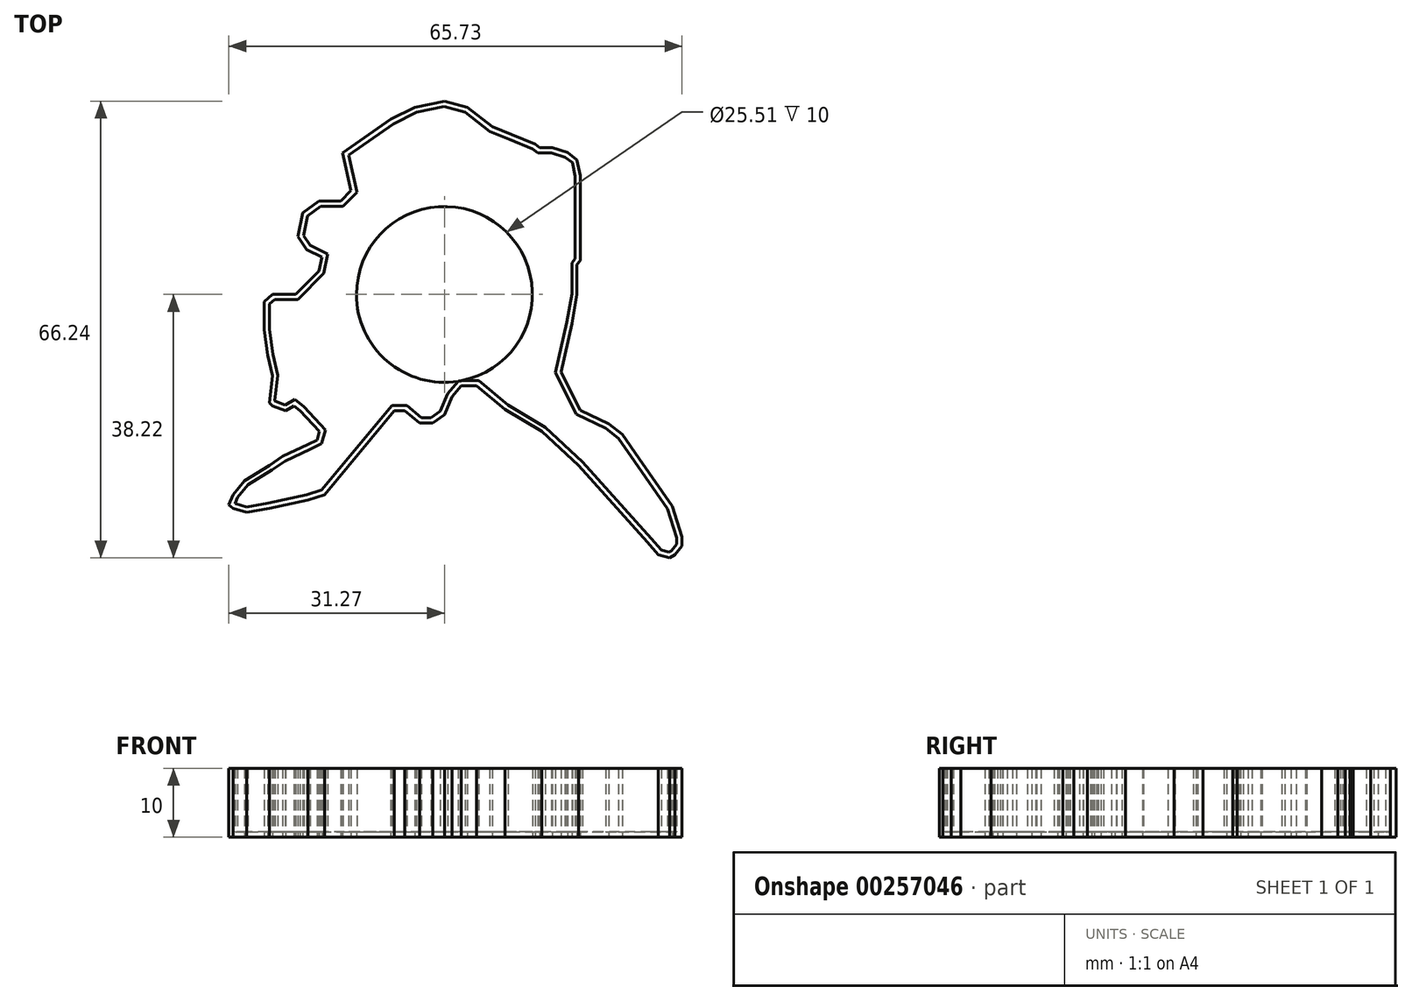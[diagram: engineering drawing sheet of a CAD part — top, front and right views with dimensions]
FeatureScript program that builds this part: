
annotation { "Feature Type Name" : "Feature", "Feature Type Description" : "" }
export const myFeature = defineFeature(function(context is Context, id is Id, definition is map)
    precondition{}
    {
        {
            var Q0;
            Q0=qCreatedBy(makeId("Top.planeOp"),FACE);
            var sketch = newSketch(context, id + "F0", { "sketchPlane" : qUnion([Q0])});
            skLineSegment(sketch, "E0", {"start": v(-14.76, 20.56) * mm, "end": v(-7.8, 25.4) * mm});
            skLineSegment(sketch, "E1", {"start": v(-7.8, 25.4) * mm, "end": v(-4.28, 27.17) * mm});
            skLineSegment(sketch, "E2", {"start": v(-4.28, 27.17) * mm, "end": v(0, 28.02) * mm});
            skLineSegment(sketch, "E3", {"start": v(0, 28.02) * mm, "end": v(3.33, 27.17) * mm});
            skLineSegment(sketch, "E4", {"start": v(3.33, 27.17) * mm, "end": v(6.95, 24.32) * mm});
            skLineSegment(sketch, "E5", {"start": v(6.95, 24.32) * mm, "end": v(9.72, 23.22) * mm});
            skLineSegment(sketch, "E6", {"start": v(9.72, 23.22) * mm, "end": v(13.2, 21.8) * mm});
            skLineSegment(sketch, "E7", {"start": v(13.2, 21.8) * mm, "end": v(13.8, 21.31) * mm});
            skLineSegment(sketch, "E8", {"start": v(13.8, 21.31) * mm, "end": v(15.64, 21.31) * mm});
            skLineSegment(sketch, "E9", {"start": v(15.64, 21.31) * mm, "end": v(17.85, 20.61) * mm});
            skLineSegment(sketch, "E10", {"start": v(17.85, 20.61) * mm, "end": v(19.23, 19.53) * mm});
            skLineSegment(sketch, "E11", {"start": v(19.23, 19.53) * mm, "end": v(19.69, 17.22) * mm});
            skLineSegment(sketch, "E12", {"start": v(19.69, 17.22) * mm, "end": v(19.69, 14.5) * mm});
            skLineSegment(sketch, "E13", {"start": v(19.69, 14.5) * mm, "end": v(19.69, 10.18) * mm});
            skLineSegment(sketch, "E14", {"start": v(19.69, 10.18) * mm, "end": v(19.69, 4.9) * mm});
            skLineSegment(sketch, "E15", {"start": v(19.69, 4.9) * mm, "end": v(19.23, 4.32) * mm});
            skLineSegment(sketch, "E16", {"start": v(19.23, 4.32) * mm, "end": v(19.23, 0) * mm});
            skLineSegment(sketch, "E17", {"start": v(19.23, 0) * mm, "end": v(18.47, -4.21) * mm});
            skLineSegment(sketch, "E18", {"start": v(18.47, -4.21) * mm, "end": v(16.88, -11.27) * mm});
            skLineSegment(sketch, "E19", {"start": v(16.88, -11.27) * mm, "end": v(19.69, -16.78) * mm});
            skLineSegment(sketch, "E20", {"start": v(19.69, -16.78) * mm, "end": v(23.8, -18.77) * mm});
            skLineSegment(sketch, "E21", {"start": v(23.8, -18.77) * mm, "end": v(25.8, -20.33) * mm});
            skLineSegment(sketch, "E22", {"start": v(25.8, -20.33) * mm, "end": v(28.2, -23.8) * mm});
            skLineSegment(sketch, "E23", {"start": v(28.2, -23.8) * mm, "end": v(33.02, -30.73) * mm});
            skLineSegment(sketch, "E24", {"start": v(33.02, -30.73) * mm, "end": v(34.46, -35.15) * mm});
            skLineSegment(sketch, "E25", {"start": v(34.46, -35.15) * mm, "end": v(34.46, -36.52) * mm});
            skLineSegment(sketch, "E26", {"start": v(34.46, -36.52) * mm, "end": v(33.4, -37.77) * mm});
            skLineSegment(sketch, "E27", {"start": v(33.4, -37.77) * mm, "end": v(32.64, -38.22) * mm});
            skLineSegment(sketch, "E28", {"start": v(32.64, -38.22) * mm, "end": v(31.03, -37.77) * mm});
            skLineSegment(sketch, "E29", {"start": v(31.03, -37.77) * mm, "end": v(29.4, -35.93) * mm});
            skLineSegment(sketch, "E30", {"start": v(29.4, -35.93) * mm, "end": v(19.48, -24.82) * mm});
            skLineSegment(sketch, "E31", {"start": v(19.48, -24.82) * mm, "end": v(14.15, -19.87) * mm});
            skLineSegment(sketch, "E32", {"start": v(14.15, -19.87) * mm, "end": v(8.79, -16.69) * mm});
            skLineSegment(sketch, "E33", {"start": v(8.79, -16.69) * mm, "end": v(4.67, -13.27) * mm});
            skLineSegment(sketch, "E34", {"start": v(4.67, -13.27) * mm, "end": v(2.4, -13.27) * mm});
            skLineSegment(sketch, "E35", {"start": v(2.4, -13.27) * mm, "end": v(1.12, -14.82) * mm});
            skLineSegment(sketch, "E36", {"start": v(1.12, -14.82) * mm, "end": v(0, -17.42) * mm});
            skLineSegment(sketch, "E37", {"start": v(0, -17.42) * mm, "end": v(-1.7, -18.66) * mm});
            skLineSegment(sketch, "E38", {"start": v(-1.7, -18.66) * mm, "end": v(-3.6, -18.66) * mm});
            skLineSegment(sketch, "E39", {"start": v(-3.6, -18.66) * mm, "end": v(-5.74, -16.88) * mm});
            skLineSegment(sketch, "E40", {"start": v(-5.74, -16.88) * mm, "end": v(-7.25, -16.88) * mm});
            skLineSegment(sketch, "E41", {"start": v(-7.25, -16.88) * mm, "end": v(-11.3, -21.74) * mm});
            skLineSegment(sketch, "E42", {"start": v(-11.3, -21.74) * mm, "end": v(-12.76, -23.5) * mm});
            skLineSegment(sketch, "E43", {"start": v(-12.76, -23.5) * mm, "end": v(-16.11, -27.53) * mm});
            skLineSegment(sketch, "E44", {"start": v(-16.11, -27.53) * mm, "end": v(-17.36, -29.04) * mm});
            skLineSegment(sketch, "E45", {"start": v(-17.36, -29.04) * mm, "end": v(-19.79, -29.82) * mm});
            skLineSegment(sketch, "E46", {"start": v(-19.79, -29.82) * mm, "end": v(-25.4, -31) * mm});
            skLineSegment(sketch, "E47", {"start": v(-25.4, -31) * mm, "end": v(-28.7, -31.63) * mm});
            skLineSegment(sketch, "E48", {"start": v(-28.7, -31.63) * mm, "end": v(-30.68, -31) * mm});
            skLineSegment(sketch, "E49", {"start": v(-30.68, -31) * mm, "end": v(-31.27, -30.51) * mm});
            skLineSegment(sketch, "E50", {"start": v(-31.27, -30.51) * mm, "end": v(-30.68, -29.04) * mm});
            skLineSegment(sketch, "E51", {"start": v(-30.68, -29.04) * mm, "end": v(-29.02, -27.04) * mm});
            skLineSegment(sketch, "E52", {"start": v(-29.02, -27.04) * mm, "end": v(-25.4, -24.82) * mm});
            skLineSegment(sketch, "E53", {"start": v(-25.4, -24.82) * mm, "end": v(-23.49, -23.5) * mm});
            skLineSegment(sketch, "E54", {"start": v(-23.49, -23.5) * mm, "end": v(-19.79, -21.74) * mm});
            skLineSegment(sketch, "E55", {"start": v(-19.79, -21.74) * mm, "end": v(-18.44, -21.1) * mm});
            skLineSegment(sketch, "E56", {"start": v(-18.44, -21.1) * mm, "end": v(-18.11, -19.87) * mm});
            skLineSegment(sketch, "E57", {"start": v(-18.11, -19.87) * mm, "end": v(-20.92, -16.88) * mm});
            skLineSegment(sketch, "E58", {"start": v(-20.92, -16.88) * mm, "end": v(-21.8, -16.14) * mm});
            skLineSegment(sketch, "E59", {"start": v(-21.8, -16.14) * mm, "end": v(-23.05, -16.88) * mm});
            skLineSegment(sketch, "E60", {"start": v(-23.05, -16.88) * mm, "end": v(-24.93, -16.14) * mm});
            skLineSegment(sketch, "E61", {"start": v(-24.93, -16.14) * mm, "end": v(-25.4, -15.76) * mm});
            skLineSegment(sketch, "E62", {"start": v(-25.4, -15.76) * mm, "end": v(-24.93, -11.78) * mm});
            skLineSegment(sketch, "E63", {"start": v(-24.93, -11.78) * mm, "end": v(-25.61, -8.8) * mm});
            skLineSegment(sketch, "E64", {"start": v(-25.61, -8.8) * mm, "end": v(-26.15, -5.12) * mm});
            skLineSegment(sketch, "E65", {"start": v(-26.15, -5.12) * mm, "end": v(-26.15, -1.06) * mm});
            skLineSegment(sketch, "E66", {"start": v(-26.15, -1.06) * mm, "end": v(-24.93, 0) * mm});
            skLineSegment(sketch, "E67", {"start": v(-24.93, 0) * mm, "end": v(-21.55, 0) * mm});
            skLineSegment(sketch, "E68", {"start": v(-21.55, 0) * mm, "end": v(-18.2, 3.42) * mm});
            skLineSegment(sketch, "E69", {"start": v(-18.2, 3.42) * mm, "end": v(-17.78, 5.42) * mm});
            skLineSegment(sketch, "E70", {"start": v(-17.78, 5.42) * mm, "end": v(-20.01, 6.53) * mm});
            skLineSegment(sketch, "E71", {"start": v(-20.01, 6.53) * mm, "end": v(-21.27, 8.38) * mm});
            skLineSegment(sketch, "E72", {"start": v(-21.27, 8.38) * mm, "end": v(-20.56, 11.83) * mm});
            skLineSegment(sketch, "E73", {"start": v(-20.56, 11.83) * mm, "end": v(-18.2, 13.53) * mm});
            skLineSegment(sketch, "E74", {"start": v(-18.2, 13.53) * mm, "end": v(-15.06, 13.53) * mm});
            skLineSegment(sketch, "E75", {"start": v(-15.06, 13.53) * mm, "end": v(-13.54, 15.05) * mm});
            skLineSegment(sketch, "E76", {"start": v(-13.54, 15.05) * mm, "end": v(-14.76, 20.56) * mm});
            skSolve(sketch);
        }
        {
            var Q0;
            Q0 = qSketchRegion(id + "F0", true);
            extrude(context, id + "F1", {"entities" : qUnion([Q0]), "depth" : 10 * mm});
        }
        {
            var Q0;
            Q0=makeQuery(id+"F1.opExtrude","CAP_FACE",FACE,{"disambiguationData":[OSD([sQuery(id+"F0.wireOp",EDGE,"E0"),sQuery(id+"F0.wireOp",EDGE,"E1"),sQuery(id+"F0.wireOp",EDGE,"E2"),sQuery(id+"F0.wireOp",EDGE,"E3"),sQuery(id+"F0.wireOp",EDGE,"E4"),sQuery(id+"F0.wireOp",EDGE,"E5"),sQuery(id+"F0.wireOp",EDGE,"E6"),sQuery(id+"F0.wireOp",EDGE,"E7"),sQuery(id+"F0.wireOp",EDGE,"E8"),sQuery(id+"F0.wireOp",EDGE,"E9"),sQuery(id+"F0.wireOp",EDGE,"E10"),sQuery(id+"F0.wireOp",EDGE,"E11"),sQuery(id+"F0.wireOp",EDGE,"E12"),sQuery(id+"F0.wireOp",EDGE,"E13"),sQuery(id+"F0.wireOp",EDGE,"E14"),sQuery(id+"F0.wireOp",EDGE,"E15"),sQuery(id+"F0.wireOp",EDGE,"E16"),sQuery(id+"F0.wireOp",EDGE,"E17"),sQuery(id+"F0.wireOp",EDGE,"E18"),sQuery(id+"F0.wireOp",EDGE,"E19"),sQuery(id+"F0.wireOp",EDGE,"E20"),sQuery(id+"F0.wireOp",EDGE,"E21"),sQuery(id+"F0.wireOp",EDGE,"E22"),sQuery(id+"F0.wireOp",EDGE,"E23"),sQuery(id+"F0.wireOp",EDGE,"E24"),sQuery(id+"F0.wireOp",EDGE,"E25"),sQuery(id+"F0.wireOp",EDGE,"E26"),sQuery(id+"F0.wireOp",EDGE,"E27"),sQuery(id+"F0.wireOp",EDGE,"E28"),sQuery(id+"F0.wireOp",EDGE,"E29"),sQuery(id+"F0.wireOp",EDGE,"E30"),sQuery(id+"F0.wireOp",EDGE,"E31"),sQuery(id+"F0.wireOp",EDGE,"E32"),sQuery(id+"F0.wireOp",EDGE,"E33"),sQuery(id+"F0.wireOp",EDGE,"E34"),sQuery(id+"F0.wireOp",EDGE,"E35"),sQuery(id+"F0.wireOp",EDGE,"E36"),sQuery(id+"F0.wireOp",EDGE,"E37"),sQuery(id+"F0.wireOp",EDGE,"E38"),sQuery(id+"F0.wireOp",EDGE,"E39"),sQuery(id+"F0.wireOp",EDGE,"E40"),sQuery(id+"F0.wireOp",EDGE,"E41"),sQuery(id+"F0.wireOp",EDGE,"E42"),sQuery(id+"F0.wireOp",EDGE,"E43"),sQuery(id+"F0.wireOp",EDGE,"E44"),sQuery(id+"F0.wireOp",EDGE,"E45"),sQuery(id+"F0.wireOp",EDGE,"E46"),sQuery(id+"F0.wireOp",EDGE,"E47"),sQuery(id+"F0.wireOp",EDGE,"E48"),sQuery(id+"F0.wireOp",EDGE,"E49"),sQuery(id+"F0.wireOp",EDGE,"E50"),sQuery(id+"F0.wireOp",EDGE,"E51"),sQuery(id+"F0.wireOp",EDGE,"E52"),sQuery(id+"F0.wireOp",EDGE,"E53"),sQuery(id+"F0.wireOp",EDGE,"E54"),sQuery(id+"F0.wireOp",EDGE,"E55"),sQuery(id+"F0.wireOp",EDGE,"E56"),sQuery(id+"F0.wireOp",EDGE,"E57"),sQuery(id+"F0.wireOp",EDGE,"E58"),sQuery(id+"F0.wireOp",EDGE,"E59"),sQuery(id+"F0.wireOp",EDGE,"E60"),sQuery(id+"F0.wireOp",EDGE,"E61"),sQuery(id+"F0.wireOp",EDGE,"E62"),sQuery(id+"F0.wireOp",EDGE,"E63"),sQuery(id+"F0.wireOp",EDGE,"E64"),sQuery(id+"F0.wireOp",EDGE,"E65"),sQuery(id+"F0.wireOp",EDGE,"E66"),sQuery(id+"F0.wireOp",EDGE,"E67"),sQuery(id+"F0.wireOp",EDGE,"E68"),sQuery(id+"F0.wireOp",EDGE,"E69"),sQuery(id+"F0.wireOp",EDGE,"E70"),sQuery(id+"F0.wireOp",EDGE,"E71"),sQuery(id+"F0.wireOp",EDGE,"E72"),sQuery(id+"F0.wireOp",EDGE,"E73"),sQuery(id+"F0.wireOp",EDGE,"E74"),sQuery(id+"F0.wireOp",EDGE,"E75"),sQuery(id+"F0.wireOp",EDGE,"E76")])],"isStart":false});
            shell(context, id + "F2", {"entities" : qUnion([Q0]), "thickness" : 0.76 * mm});
        }
        {
            var Q0;
            Q0=makeQuery(id+"F1.opExtrude","CAP_FACE",FACE,{"disambiguationData":[OSD([sQuery(id+"F0.wireOp",EDGE,"E0"),sQuery(id+"F0.wireOp",EDGE,"E1"),sQuery(id+"F0.wireOp",EDGE,"E2"),sQuery(id+"F0.wireOp",EDGE,"E3"),sQuery(id+"F0.wireOp",EDGE,"E4"),sQuery(id+"F0.wireOp",EDGE,"E5"),sQuery(id+"F0.wireOp",EDGE,"E6"),sQuery(id+"F0.wireOp",EDGE,"E7"),sQuery(id+"F0.wireOp",EDGE,"E8"),sQuery(id+"F0.wireOp",EDGE,"E9"),sQuery(id+"F0.wireOp",EDGE,"E10"),sQuery(id+"F0.wireOp",EDGE,"E11"),sQuery(id+"F0.wireOp",EDGE,"E12"),sQuery(id+"F0.wireOp",EDGE,"E13"),sQuery(id+"F0.wireOp",EDGE,"E14"),sQuery(id+"F0.wireOp",EDGE,"E15"),sQuery(id+"F0.wireOp",EDGE,"E16"),sQuery(id+"F0.wireOp",EDGE,"E17"),sQuery(id+"F0.wireOp",EDGE,"E18"),sQuery(id+"F0.wireOp",EDGE,"E19"),sQuery(id+"F0.wireOp",EDGE,"E20"),sQuery(id+"F0.wireOp",EDGE,"E21"),sQuery(id+"F0.wireOp",EDGE,"E22"),sQuery(id+"F0.wireOp",EDGE,"E23"),sQuery(id+"F0.wireOp",EDGE,"E24"),sQuery(id+"F0.wireOp",EDGE,"E25"),sQuery(id+"F0.wireOp",EDGE,"E26"),sQuery(id+"F0.wireOp",EDGE,"E27"),sQuery(id+"F0.wireOp",EDGE,"E28"),sQuery(id+"F0.wireOp",EDGE,"E29"),sQuery(id+"F0.wireOp",EDGE,"E30"),sQuery(id+"F0.wireOp",EDGE,"E31"),sQuery(id+"F0.wireOp",EDGE,"E32"),sQuery(id+"F0.wireOp",EDGE,"E33"),sQuery(id+"F0.wireOp",EDGE,"E34"),sQuery(id+"F0.wireOp",EDGE,"E35"),sQuery(id+"F0.wireOp",EDGE,"E36"),sQuery(id+"F0.wireOp",EDGE,"E37"),sQuery(id+"F0.wireOp",EDGE,"E38"),sQuery(id+"F0.wireOp",EDGE,"E39"),sQuery(id+"F0.wireOp",EDGE,"E40"),sQuery(id+"F0.wireOp",EDGE,"E41"),sQuery(id+"F0.wireOp",EDGE,"E42"),sQuery(id+"F0.wireOp",EDGE,"E43"),sQuery(id+"F0.wireOp",EDGE,"E44"),sQuery(id+"F0.wireOp",EDGE,"E45"),sQuery(id+"F0.wireOp",EDGE,"E46"),sQuery(id+"F0.wireOp",EDGE,"E47"),sQuery(id+"F0.wireOp",EDGE,"E48"),sQuery(id+"F0.wireOp",EDGE,"E49"),sQuery(id+"F0.wireOp",EDGE,"E50"),sQuery(id+"F0.wireOp",EDGE,"E51"),sQuery(id+"F0.wireOp",EDGE,"E52"),sQuery(id+"F0.wireOp",EDGE,"E53"),sQuery(id+"F0.wireOp",EDGE,"E54"),sQuery(id+"F0.wireOp",EDGE,"E55"),sQuery(id+"F0.wireOp",EDGE,"E56"),sQuery(id+"F0.wireOp",EDGE,"E57"),sQuery(id+"F0.wireOp",EDGE,"E58"),sQuery(id+"F0.wireOp",EDGE,"E59"),sQuery(id+"F0.wireOp",EDGE,"E60"),sQuery(id+"F0.wireOp",EDGE,"E61"),sQuery(id+"F0.wireOp",EDGE,"E62"),sQuery(id+"F0.wireOp",EDGE,"E63"),sQuery(id+"F0.wireOp",EDGE,"E64"),sQuery(id+"F0.wireOp",EDGE,"E65"),sQuery(id+"F0.wireOp",EDGE,"E66"),sQuery(id+"F0.wireOp",EDGE,"E67"),sQuery(id+"F0.wireOp",EDGE,"E68"),sQuery(id+"F0.wireOp",EDGE,"E69"),sQuery(id+"F0.wireOp",EDGE,"E70"),sQuery(id+"F0.wireOp",EDGE,"E71"),sQuery(id+"F0.wireOp",EDGE,"E72"),sQuery(id+"F0.wireOp",EDGE,"E73"),sQuery(id+"F0.wireOp",EDGE,"E74"),sQuery(id+"F0.wireOp",EDGE,"E75"),sQuery(id+"F0.wireOp",EDGE,"E76")])],"isStart":true});
            var sketch = newSketch(context, id + "F3", { "sketchPlane" : qUnion([Q0])});
            skCircle(sketch, "E77", {"center": v(0, 0) * mm, "radius": 12.76 * mm});
            skSolve(sketch);
        }
        {
            var Q0;
            Q0 = qSketchRegion(id + "F3", true);
            extrude(context, id + "F4", {"entities" : qUnion([Q0]), "operationType" : NewBodyOperationType.REMOVE, "oppositeDirection" : true, "depth" : 25.4 * mm});
        }
    });
